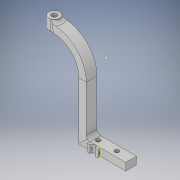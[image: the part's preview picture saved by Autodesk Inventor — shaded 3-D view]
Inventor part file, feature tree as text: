
AUTODESK INVENTOR PART (.ipt)
format: ipt  version: 2017 (Build 210142000, 142)  size: 222,720 bytes
history: native  units: in
note: dims shown in document units (in); Inventor stores cm internally (conversion verified against a paired STEP export)
features: sketch x7, fillet x2, extrude x2, revolve x1, plane x1, sweep x1, hole x1, projected_geometry x1
ambient origin geometry x8: Origin, YZ Plane, XZ Plane, XY Plane, X Axis, Y Axis, Z Axis, Center Point
bodies: Solid1 (feature_tree)
feature tree (16):
  revolve  "Revolution1"  [1 undecoded]
  plane  "Work Plane1"
  sweep  "Sweep1"
  fillet  "Fillet1"  Radius=0.1875in
  hole  "Hole1"  [1 undecoded]
  fillet  "Fillet2"  Radius=1.5in
  extrude  "Extrusion1"  Depth=2.0in
  extrude  "Extrusion2"  Depth=0.15in
  sketch  "Sketch7"  dims[d14=0.205in d15=0.75in d16=0.375in d17=0.25in d18=0.5635in d19=1.0in d20=0.8108in d21=0.18in d22=0.26in d23=0.36in d24=0.0in d25=0.86in d26=0.0in]
  sketch  "Sketch1"  dims[d0=0.12in d1=0.13in]
  sketch  "Sketch2"  dims[d2=0.13in d3=90.0deg d4=0.1875in]
  projected_geometry  "Projected Loop1"
  sketch  "Sketch3"  dims[d5=0.16in d6=0.2in d7=1.5in]
  sketch  "Sketch4"  dims[d8=2.5in d9=2.0in]
  sketch  "Sketch5"  dims[d10=0.0in d11=0.0in d12=0.15in]
  sketch  "Sketch6"  dims[d13=0.45in]
note: 2 required parameter values undecoded (feature->parameter linkage not recoverable at this tier; creation-order binding heuristic only, values carry confidence <= 0.55)